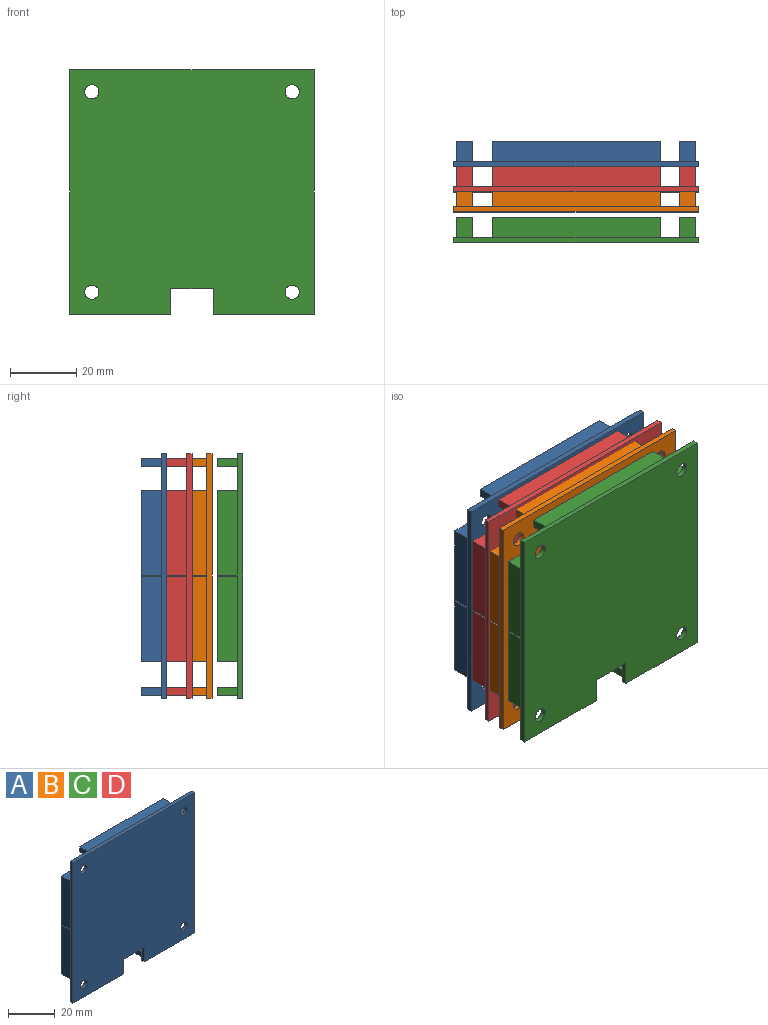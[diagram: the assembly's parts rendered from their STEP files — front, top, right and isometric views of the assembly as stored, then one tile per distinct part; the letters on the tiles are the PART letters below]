
ASSEMBLY  parts=4 mates=6
PART A: 44 faces, bbox 73.7x7.6x73.7 mm
  f0: plane 73.66x73.66mm, normal (0,1,0), area 4586.6mm2, adj f1,f2,f3,f4,f5,f6,f7,f8
  f1: plane 73.66x1.57mm, normal (-1,0,0), area 116mm2, adj f0,f2,f8,f9
  f2: plane 30.48x1.57mm, normal (0,0,-1), area 48mm2, adj f0,f1,f3,f9
  f3: plane 7.62x1.57mm, normal (1,0,0), area 12mm2, adj f0,f2,f4,f9
  f4: plane 12.7x1.57mm, normal (0,0,-1), area 20mm2, adj f0,f3,f5,f9
  f5: plane 7.62x1.57mm, normal (-1,0,0), area 12mm2, adj f0,f4,f6,f9
  f6: plane 30.48x1.57mm, normal (0,0,-1), area 48mm2, adj f0,f5,f7,f9
  f7: plane 73.66x1.57mm, normal (1,0,0), area 116mm2, adj f0,f6,f8,f9
  f8: plane 73.66x1.57mm, normal (0,0,1), area 116mm2, adj f0,f1,f7,f9
  f9: plane 73.66x73.66mm, normal (0,-1,0), area 5270.4mm2, adj f1,f2,f3,f4,f5,f6,f7,f8
  f10: cylinder r=2.16mm len=4.32mm, axis (0,-1,0), area 21.4mm2, adj f0,f9
  f11: cylinder r=2.16mm len=4.32mm, axis (0,-1,0), area 21.4mm2, adj f0,f9
  f12: cylinder r=2.16mm len=4.32mm, axis (0,-1,0), area 21.4mm2, adj f0,f9
  f13: cylinder r=2.16mm len=4.32mm, axis (0,-1,0), area 21.4mm2, adj f0,f9
  f14: plane 6.05x5.08mm, normal (0,0,1), area 30.7mm2, adj f0,f15,f17,f18
  f15: plane 25.4x6.05mm, normal (-1,0,0), area 153.5mm2, adj f0,f14,f16,f18
  f16: plane 6.05x5.08mm, normal (0,0,-1), area 30.7mm2, adj f0,f15,f17,f18
  f17: plane 25.4x6.05mm, normal (1,0,0), area 153.5mm2, adj f0,f14,f16,f18
  f18: plane 25.4x5.08mm, normal (0,1,0), area 129mm2, adj f14,f15,f16,f17
  f19: plane 6.05x5.08mm, normal (0,0,1), area 30.7mm2, adj f0,f20,f22,f23
  f20: plane 25.4x6.05mm, normal (-1,0,0), area 153.5mm2, adj f0,f19,f21,f23
  f21: plane 6.05x5.08mm, normal (0,0,-1), area 30.7mm2, adj f0,f20,f22,f23
  f22: plane 25.4x6.05mm, normal (1,0,0), area 153.5mm2, adj f0,f19,f21,f23
  f23: plane 25.4x5.08mm, normal (0,1,0), area 129mm2, adj f19,f20,f21,f22
  f24: plane 50.8x6.05mm, normal (0,0,1), area 307.1mm2, adj f0,f25,f27,f28
  f25: plane 6.05x2.54mm, normal (-1,0,0), area 15.4mm2, adj f0,f24,f26,f28
  f26: plane 50.8x6.05mm, normal (0,0,-1), area 307.1mm2, adj f0,f25,f27,f28
  f27: plane 6.05x2.54mm, normal (1,0,0), area 15.4mm2, adj f0,f24,f26,f28
  f28: plane 50.8x2.54mm, normal (0,1,0), area 129mm2, adj f24,f25,f26,f27
  f29: plane 6.05x5.08mm, normal (0,0,1), area 30.7mm2, adj f0,f30,f32,f33
  f30: plane 25.4x6.05mm, normal (-1,0,0), area 153.5mm2, adj f0,f29,f31,f33
  f31: plane 6.05x5.08mm, normal (0,0,-1), area 30.7mm2, adj f0,f30,f32,f33
  f32: plane 25.4x6.05mm, normal (1,0,0), area 153.5mm2, adj f0,f29,f31,f33
  f33: plane 25.4x5.08mm, normal (0,1,0), area 129mm2, adj f29,f30,f31,f32
  f34: plane 6.05x5.08mm, normal (0,0,1), area 30.7mm2, adj f0,f35,f37,f38
  f35: plane 25.4x6.05mm, normal (-1,0,0), area 153.5mm2, adj f0,f34,f36,f38
  f36: plane 6.05x5.08mm, normal (0,0,-1), area 30.7mm2, adj f0,f35,f37,f38
  f37: plane 25.4x6.05mm, normal (1,0,0), area 153.5mm2, adj f0,f34,f36,f38
  f38: plane 25.4x5.08mm, normal (0,1,0), area 129mm2, adj f34,f35,f36,f37
  f39: plane 15.24x6.05mm, normal (0,0,1), area 92.1mm2, adj f0,f40,f42,f43
  f40: plane 6.05x2.54mm, normal (-1,0,0), area 15.4mm2, adj f0,f39,f41,f43
  f41: plane 15.24x6.05mm, normal (0,0,-1), area 92.1mm2, adj f0,f40,f42,f43
  f42: plane 6.05x2.54mm, normal (1,0,0), area 15.4mm2, adj f0,f39,f41,f43
  f43: plane 15.24x2.54mm, normal (0,1,0), area 38.7mm2, adj f39,f40,f41,f42
PART B: same geometry as A
PART C: same geometry as A
PART D: same geometry as A
PLACE A t=(30.18,15.58,-47.12)mm
PLACE B t=(30.18,1.91,-47.12)mm
PLACE C t=(30.18,-7.28,-47.12)mm
PLACE D t=(30.18,7.96,-47.12)mm
MATE revolute C.f10 <-> A.f10  axis (0,-1,0) through (36.79,-7.28,-40.51)mm
MATE revolute B.f10 <-> A.f10  axis (0,-1,0) through (36.79,1.91,-40.51)mm
MATE revolute C.f11 <-> B.f11  axis (0,-1,0) through (97.24,-5.71,19.94)mm
MATE revolute C.f11 <-> A.f11  axis (0,-1,0) through (97.24,-5.71,19.94)mm
MATE revolute D.f10 <-> A.f10  axis (0,-1,0) through (36.79,8.75,-40.51)mm
MATE revolute C.f11 <-> D.f11  axis (0,-1,0) through (97.24,-6.49,19.94)mm
